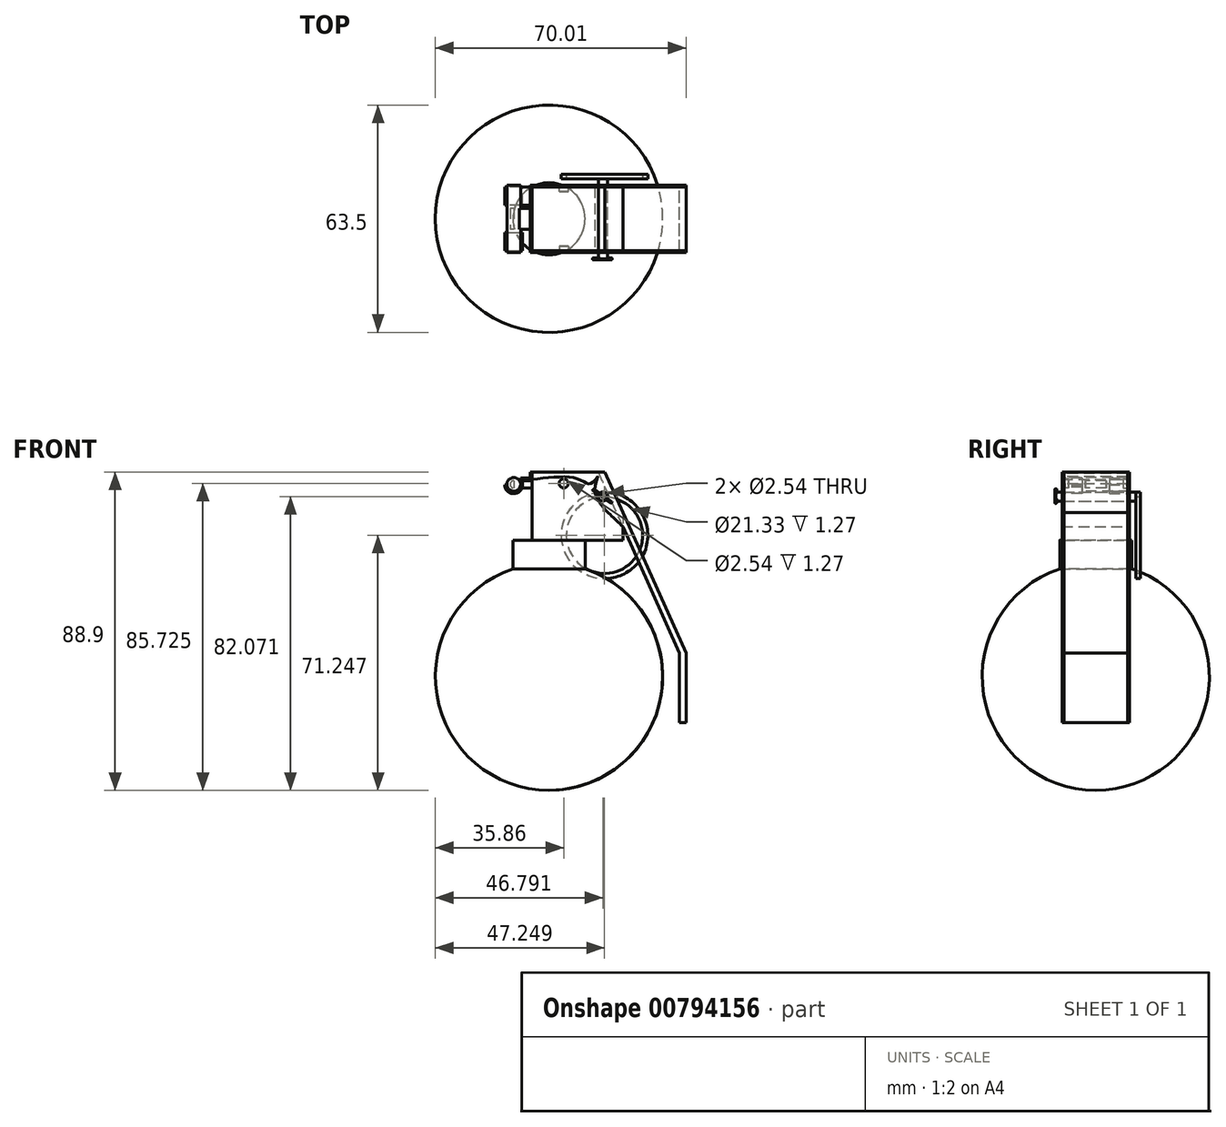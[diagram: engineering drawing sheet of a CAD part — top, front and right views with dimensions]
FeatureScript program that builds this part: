
annotation { "Feature Type Name" : "Feature", "Feature Type Description" : "" }
export const myFeature = defineFeature(function(context is Context, id is Id, definition is map)
    precondition{}
    {
        {
            var Q0;
            Q0=qCreatedBy(makeId("Front.planeOp"),FACE);
            var sketch = newSketch(context, id + "F0", { "sketchPlane" : qUnion([Q0])});
            skCircle(sketch, "E0", {"center": v(0, 0) * mm, "radius": 31.75 * mm});
            skLineSegment(sketch, "E1", {"start": v(0, 31.75) * mm, "end": v(0, -31.75) * mm});
            skSolve(sketch);
        }
        {
            var Q0;
            {var subQ0=sQuery(id+"F0.wireOp",EDGE,"E1");Q0=makeQuery(id+"F0.imprint","IMPRINT",FACE,{"disambiguationData":[TD([[makeQuery(id+"F0.imprint","IMPRINT",EDGE,{"derivedFrom":subQ0}),-1.0]])]});}
            var Q1;
            Q1=sQuery(id+"F0.wireOp",EDGE,"E1");
            revolve(context, id + "F1", {"surfaceOperationType" : NewSurfaceOperationType.NEW, "entities" : qUnion([Q0]), "axis" : qUnion([Q1]), "revolveType" : RevolveType.FULL});
        }
        {
            var Q0;
            Q0=qCreatedBy(makeId("Top.planeOp"),FACE);
            var sketch = newSketch(context, id + "F2", { "sketchPlane" : qUnion([Q0])});
            skCircle(sketch, "E2", {"center": v(0, 0) * mm, "radius": 10.07 * mm});
            skSolve(sketch);
        }
        {
            var Q0;
            Q0 = qSketchRegion(id + "F2", true);
            extrude(context, id + "F3", {"entities" : qUnion([Q0]), "operationType" : NewBodyOperationType.ADD, "depth" : 38.1 * mm, "offsetDistance" : 25.4 * mm});
        }
        {
            var Q0;
            Q0=makeQuery(id+"F3.opExtrude","CAP_FACE",FACE,{"disambiguationData":[OSD([sQuery(id+"F2.wireOp",EDGE,"E2")])],"isStart":false});
            var sketch = newSketch(context, id + "F4", { "sketchPlane" : qUnion([Q0])});
            skLineSegment(sketch, "E3.bottom", {"start": v(-4.78, 8.87) * mm, "end": v(20.62, 8.87) * mm});
            skLineSegment(sketch, "E3.top", {"start": v(-4.78, -8.87) * mm, "end": v(20.62, -8.87) * mm});
            skLineSegment(sketch, "E3.left", {"start": v(-4.78, 8.87) * mm, "end": v(-4.78, -8.87) * mm});
            skLineSegment(sketch, "E3.right", {"start": v(20.62, 8.87) * mm, "end": v(20.62, -8.87) * mm});
            skSolve(sketch);
        }
        {
            var Q0;
            {var subQ0=sQuery(id+"F4.wireOp",EDGE,"E3.left");Q0=makeQuery(id+"F4.imprint","IMPRINT",FACE,{"disambiguationData":[TD([[makeQuery(id+"F4.imprint","IMPRINT",EDGE,{"derivedFrom":subQ0}),1.0]])]});}
            var Q1;
            {var subQ0=sQuery(id+"F4.wireOp",EDGE,"E3.right");Q1=makeQuery(id+"F4.imprint","IMPRINT",FACE,{"disambiguationData":[TD([[makeQuery(id+"F4.imprint","IMPRINT",EDGE,{"derivedFrom":subQ0}),-1.0]])]});}
            extrude(context, id + "F5", {"entities" : qUnion([Q0, Q1]), "operationType" : NewBodyOperationType.ADD, "depth" : 19.05 * mm, "offsetDistance" : 25.4 * mm});
        }
        {
            var Q0;
            Q0=makeQuery(id+"F5.opExtrude","SWEPT_FACE",FACE,{"disambiguationData":[OSD([sQuery(id+"F4.wireOp",EDGE,"E3.bottom")])]});
            var sketch = newSketch(context, id + "F6", { "sketchPlane" : qUnion([Q0])});
            skLineSegment(sketch, "E4", {"start": v(-20.62, 41.9) * mm, "end": v(-13.77, 57.15) * mm});
            skLineSegment(sketch, "E5", {"start": v(-13.77, 57.15) * mm, "end": v(-15.54, 57.15) * mm});
            skLineSegment(sketch, "E6", {"start": v(-15.54, 57.15) * mm, "end": v(-38.26, 6.55) * mm});
            skLineSegment(sketch, "E7", {"start": v(-38.26, 6.55) * mm, "end": v(-38.26, -12.78) * mm});
            skLineSegment(sketch, "E8", {"start": v(-38.26, -12.78) * mm, "end": v(-36.4, -12.78) * mm});
            skLineSegment(sketch, "E9", {"start": v(-36.4, -12.78) * mm, "end": v(-36.4, 6.55) * mm});
            skLineSegment(sketch, "E10", {"start": v(-36.4, 6.55) * mm, "end": v(-20.62, 41.9) * mm});
            skPoint(sketch, "E11.4.internal.snap0", {"position": v(-7.92, 57.15) * mm});
            skFitSpline(sketch, "E11", {"points": [v(-20.62, 41.9) * mm, v(-12.84, 51.9) * mm, v(-13.59, 55.87) * mm, v(-11.77, 53.97) * mm, v(-7.92, 55.3) * mm, v(4.78, 55.13) * mm], "startDerivative": vector(37.94, 36.96) * mm, "endDerivative": vector(48.27, -4.72) * mm});
            skCircle(sketch, "E12", {"center": v(-15.04, 50.32) * mm, "radius": 1.27 * mm});
            skSolve(sketch);
        }
        {
            var Q0;
            Q0 = qSketchRegion(id + "F6", true);
            extrude(context, id + "F7", {"entities" : qUnion([Q0]), "oppositeDirection" : true, "depth" : 17.78 * mm, "offsetDistance" : 25.4 * mm});
        }
        {
            var Q0;
            {var subQ0=sQuery(id+"F6.wireOp",EDGE,"E6");var subQ1=sQuery(id+"F4.wireOp",EDGE,"E3.bottom");var subQ2=makeQuery(id+"F5.opExtrude","CAP_EDGE",EDGE,{"disambiguationData":[OSD([subQ1])],"isStart":false});var subQ3=makeQuery(id+"F6.imprint","INTERSECT",VERTEX,{"derivedFrom":[subQ2,sQuery(id+"F6.wireOp",EDGE,"E5"),subQ0]});Q0=makeQuery(id+"F6.imprint","IMPRINT",FACE,{"disambiguationData":[TD([[makeQuery(id+"F6.imprint","IMPRINT",EDGE,{"disambiguationData":[TD([[subQ3,-1.0]])],"derivedFrom":subQ0}),-1.0]])]});}
            extrude(context, id + "F8", {"entities" : qUnion([Q0]), "operationType" : NewBodyOperationType.REMOVE, "oppositeDirection" : true, "depth" : 25.4 * mm, "offsetDistance" : 25.4 * mm});
        }
        {
            var Q0;
            {var subQ0=sQuery(id+"F6.wireOp",EDGE,"E4");Q0=makeQuery(id+"F6.imprint","IMPRINT",FACE,{"disambiguationData":[TD([[makeQuery(id+"F6.imprint","IMPRINT",EDGE,{"derivedFrom":subQ0}),1.0]])]});}
            var Q1;
            {var subQ0=sQuery(id+"F6.wireOp",EDGE,"E4");Q1=makeQuery(id+"F6.imprint","IMPRINT",FACE,{"disambiguationData":[TD([[makeQuery(id+"F6.imprint","IMPRINT",EDGE,{"derivedFrom":subQ0}),-1.0]])]});}
            var Q2;
            {var subQ0=sQuery(id+"F6.wireOp",EDGE,"E7");Q2=makeQuery(id+"F6.imprint","IMPRINT",FACE,{"disambiguationData":[TD([[makeQuery(id+"F6.imprint","IMPRINT",EDGE,{"derivedFrom":subQ0}),1.0]])]});}
            extrude(context, id + "F9", {"entities" : qUnion([Q0, Q1, Q2]), "depth" : 0.5 * mm, "offsetDistance" : 25.4 * mm});
        }
        {
            var Q0;
            {var subQ0=sQuery(id+"F6.wireOp",EDGE,"E4");Q0=makeQuery(id+"F6.imprint","IMPRINT",FACE,{"disambiguationData":[TD([[makeQuery(id+"F6.imprint","IMPRINT",EDGE,{"derivedFrom":subQ0}),-1.0]])]});}
            var Q1;
            {var subQ0=sQuery(id+"F6.wireOp",EDGE,"E4");Q1=makeQuery(id+"F6.imprint","IMPRINT",FACE,{"disambiguationData":[TD([[makeQuery(id+"F6.imprint","IMPRINT",EDGE,{"derivedFrom":subQ0}),1.0]])]});}
            var Q2;
            {var subQ0=sQuery(id+"F6.wireOp",EDGE,"E7");Q2=makeQuery(id+"F6.imprint","IMPRINT",FACE,{"disambiguationData":[TD([[makeQuery(id+"F6.imprint","IMPRINT",EDGE,{"derivedFrom":subQ0}),1.0]])]});}
            extrude(context, id + "F10", {"entities" : qUnion([Q0, Q1, Q2]), "oppositeDirection" : true, "depth" : 18.29 * mm, "offsetDistance" : 25.4 * mm});
        }
        {
            var Q0;
            Q0=makeQuery(id+"F5.opExtrude","SWEPT_FACE",FACE,{"disambiguationData":[OSD([sQuery(id+"F4.wireOp",EDGE,"E3.left")])]});
            var sketch = newSketch(context, id + "F11", { "sketchPlane" : qUnion([Q0])});
            skLineSegment(sketch, "E13", {"start": v(-9.66, 56.79) * mm, "end": v(9.7, 56.79) * mm});
            skLineSegment(sketch, "E14.bottom", {"start": v(-2.95, 54.72) * mm, "end": v(2.95, 54.72) * mm});
            skLineSegment(sketch, "E14.top", {"start": v(-2.95, 52.7) * mm, "end": v(2.95, 52.7) * mm});
            skLineSegment(sketch, "E14.left", {"start": v(-2.95, 54.72) * mm, "end": v(-2.95, 52.7) * mm});
            skLineSegment(sketch, "E14.right", {"start": v(2.95, 54.72) * mm, "end": v(2.95, 52.7) * mm});
            skPoint(sketch, "E14.middle", {"position": v(0, 53.71) * mm});
            skSolve(sketch);
        }
        {
            var Q0;
            Q0=makeQuery(id+"F9.opExtrude","SWEPT_FACE",FACE,{"disambiguationData":[OSD([sQuery(id+"F2.wireOp",EDGE,"E2"),sQuery(id+"F4.wireOp",EDGE,"E3.bottom"),sQuery(id+"F4.wireOp",EDGE,"E3.left")])]});
            var Q1;
            {var subQ1=sQuery(id+"F4.wireOp",EDGE,"E3.left");var subQ7=makeQuery(id+"F5.opExtrude","CAP_EDGE",EDGE,{"disambiguationData":[OSD([subQ1])],"isStart":false});Q1=makeQuery(id+"F11.imprint","IMPRINT",FACE,{"disambiguationData":[TD([[makeQuery(id+"F11.imprint","IMPRINT",EDGE,{"derivedFrom":subQ7}),-1.0]])]});}
            var Q2;
            Q2=makeQuery(id+"F10.opExtrude","SWEPT_FACE",FACE,{"disambiguationData":[OSD([sQuery(id+"F2.wireOp",EDGE,"E2"),sQuery(id+"F4.wireOp",EDGE,"E3.bottom"),sQuery(id+"F4.wireOp",EDGE,"E3.left")])]});
            extrude(context, id + "F12", {"entities" : qUnion([Q0, Q1, Q2]), "depth" : 0.5 * mm, "offsetDistance" : 25.4 * mm});
        }
        {
            var Q0;
            Q0=makeQuery(id+"F11.imprint","IMPRINT",FACE,{"disambiguationData":[TD([[makeQuery(id+"F11.imprint","IMPRINT",EDGE,{"derivedFrom":sQuery(id+"F11.wireOp",EDGE,"E14.bottom")}),-1.0]])]});
            extrude(context, id + "F13", {"entities" : qUnion([Q0]), "operationType" : NewBodyOperationType.ADD, "depth" : 5.08 * mm, "offsetDistance" : 25.4 * mm});
        }
        {
            var Q0;
            Q0=makeQuery(id+"F13.opExtrude","CAP_FACE",FACE,{"disambiguationData":[OSD([sQuery(id+"F11.wireOp",EDGE,"E14.bottom"),sQuery(id+"F11.wireOp",EDGE,"E14.top"),sQuery(id+"F11.wireOp",EDGE,"E14.left"),sQuery(id+"F11.wireOp",EDGE,"E14.right")])],"isStart":false});
            var sketch = newSketch(context, id + "F14", { "sketchPlane" : qUnion([Q0])});
            skLineSegment(sketch, "E15", {"start": v(-2.95, 53.71) * mm, "end": v(2.95, 53.71) * mm});
            skLineSegment(sketch, "E16", {"start": v(2.95, 53.71) * mm, "end": v(9.42, 53.71) * mm});
            skLineSegment(sketch, "E17", {"start": v(9.42, 53.71) * mm, "end": v(-9.38, 53.71) * mm});
            skLineSegment(sketch, "E18", {"start": v(-9.38, 53.71) * mm, "end": v(-9.38, 51.8) * mm});
            skLineSegment(sketch, "E19", {"start": v(-9.38, 51.8) * mm, "end": v(9.42, 51.8) * mm});
            skLineSegment(sketch, "E20", {"start": v(9.42, 53.71) * mm, "end": v(9.42, 51.8) * mm});
            skSolve(sketch);
        }
        {
            var Q0;
            {var subQ0=sQuery(id+"F14.wireOp",EDGE,"E18");Q0=makeQuery(id+"F14.imprint","IMPRINT",FACE,{"disambiguationData":[TD([[makeQuery(id+"F14.imprint","IMPRINT",EDGE,{"derivedFrom":subQ0}),1.0]])]});}
            var Q1;
            Q1=sQuery(id+"F14.wireOp",EDGE,"E17");
            revolve(context, id + "F15", {"operationType" : NewBodyOperationType.ADD, "surfaceOperationType" : NewSurfaceOperationType.NEW, "entities" : qUnion([Q0]), "axis" : qUnion([Q1]), "revolveType" : RevolveType.FULL});
        }
        {
            var Q0;
            Q0=makeQuery(id+"F5.opExtrude","SWEPT_FACE",FACE,{"disambiguationData":[OSD([sQuery(id+"F4.wireOp",EDGE,"E3.bottom")])]});
            var sketch = newSketch(context, id + "F16", { "sketchPlane" : qUnion([Q0])});
            skLineSegment(sketch, "E21.left", {"start": v(4.78, 57.15) * mm, "end": v(4.78, 55.04) * mm});
            skArc(sketch, "E22", {"start": v(7.95, 53.66) * mm, "mid": v(9.85, 51.83) * mm, "end": v(11.78, 53.63) * mm});
            skArc(sketch, "E23", {"start": v(7.4, 53.64) * mm, "mid": v(9.87, 51.12) * mm, "end": v(12.38, 53.59) * mm});
            skLineSegment(sketch, "E24", {"start": v(7.95, 53.66) * mm, "end": v(7.4, 53.64) * mm});
            skLineSegment(sketch, "E25", {"start": v(11.78, 53.63) * mm, "end": v(12.38, 53.59) * mm});
            skLineSegment(sketch, "E26.bottom", {"start": v(4.78, 55.14) * mm, "end": v(7.4, 55.14) * mm});
            skLineSegment(sketch, "E26.top", {"start": v(4.78, 55.53) * mm, "end": v(7.4, 55.53) * mm});
            skLineSegment(sketch, "E26.left", {"start": v(4.78, 55.14) * mm, "end": v(4.78, 55.53) * mm});
            skLineSegment(sketch, "E26.right", {"start": v(7.4, 55.14) * mm, "end": v(7.4, 55.53) * mm});
            skLineSegment(sketch, "E27.bottom", {"start": v(7.4, 55.53) * mm, "end": v(7.95, 55.53) * mm});
            skLineSegment(sketch, "E27.top", {"start": v(7.4, 53.66) * mm, "end": v(7.95, 53.66) * mm});
            skLineSegment(sketch, "E27.left", {"start": v(7.4, 55.53) * mm, "end": v(7.4, 53.66) * mm});
            skLineSegment(sketch, "E27.right", {"start": v(7.95, 55.53) * mm, "end": v(7.95, 53.66) * mm});
            skLineSegment(sketch, "E28", {"start": v(7.4, 53.66) * mm, "end": v(7.4, 53.64) * mm});
            skCircle(sketch, "E29", {"center": v(-4.11, 53.98) * mm, "radius": 1.27 * mm});
            skPoint(sketch, "E29.first.point", {"position": v(-4.07, 55.24) * mm});
            skPoint(sketch, "E29.second.point", {"position": v(-5.25, 53.4) * mm});
            skPoint(sketch, "E29.third.point", {"position": v(-2.9, 53.56) * mm});
            skSolve(sketch);
        }
        {
            var Q0;
            {var subQ0=sQuery(id+"F16.wireOp",EDGE,"E26.bottom");Q0=makeQuery(id+"F16.imprint","IMPRINT",FACE,{"disambiguationData":[TD([[makeQuery(id+"F16.imprint","IMPRINT",EDGE,{"derivedFrom":subQ0}),1.0]])]});}
            var Q1;
            {var subQ3=sQuery(id+"F16.wireOp",EDGE,"E27.bottom");Q1=makeQuery(id+"F16.imprint","IMPRINT",FACE,{"disambiguationData":[TD([[makeQuery(id+"F16.imprint","IMPRINT",EDGE,{"derivedFrom":subQ3}),-1.0]])]});}
            var Q2;
            Q2=makeQuery(id+"F16.imprint","IMPRINT",FACE,{"disambiguationData":[TD([[makeQuery(id+"F16.imprint","IMPRINT",EDGE,{"derivedFrom":sQuery(id+"F16.wireOp",EDGE,"E22")}),-1.0]])]});
            extrude(context, id + "F17", {"entities" : qUnion([Q0, Q1, Q2]), "oppositeDirection" : true, "depth" : 5.08 * mm, "offsetDistance" : 25.4 * mm});
        }
        {
            var Q0;
            Q0=makeQuery(id+"F5.opExtrude","SWEPT_FACE",FACE,{"disambiguationData":[OSD([sQuery(id+"F4.wireOp",EDGE,"E3.top")])]});
            var sketch = newSketch(context, id + "F18", { "sketchPlane" : qUnion([Q0])});
            skCircle(sketch, "E30", {"center": v(13.74, 50.52) * mm, "radius": 1.14 * mm});
            skPoint(sketch, "E30.first.point", {"position": v(13.7, 51.66) * mm});
            skPoint(sketch, "E30.second.point", {"position": v(13.1, 49.57) * mm});
            skPoint(sketch, "E30.third.point", {"position": v(14.83, 50.19) * mm});
            skCircle(sketch, "E31", {"center": v(4.11, 53.98) * mm, "radius": 1.27 * mm});
            skPoint(sketch, "E31.first.point", {"position": v(4.27, 55.24) * mm});
            skPoint(sketch, "E31.second.point", {"position": v(2.96, 53.44) * mm});
            skPoint(sketch, "E31.third.point", {"position": v(5.2, 53.32) * mm});
            skLineSegment(sketch, "E32.MirrorCS", {"start": v(-7.4, 55.13) * mm, "end": v(-7.4, 55.53) * mm});
            skLineSegment(sketch, "E33.MirrorCS", {"start": v(-7.95, 53.65) * mm, "end": v(-7.4, 53.63) * mm});
            skLineSegment(sketch, "E34.MirrorCS", {"start": v(-7.4, 53.65) * mm, "end": v(-7.95, 53.65) * mm});
            skLineSegment(sketch, "E35.MirrorCS", {"start": v(-7.4, 53.65) * mm, "end": v(-7.4, 53.63) * mm});
            skLineSegment(sketch, "E36.MirrorCS", {"start": v(-7.4, 55.53) * mm, "end": v(-7.95, 55.53) * mm});
            skLineSegment(sketch, "E37.MirrorCS", {"start": v(-11.77, 53.62) * mm, "end": v(-12.37, 53.58) * mm});
            skLineSegment(sketch, "E38.MirrorCS", {"start": v(-4.77, 55.13) * mm, "end": v(-4.77, 55.53) * mm});
            skLineSegment(sketch, "E39.MirrorCS", {"start": v(-4.77, 55.13) * mm, "end": v(-7.4, 55.13) * mm});
            skArc(sketch, "E40.MirrorCS", {"start": v(-7.95, 53.65) * mm, "mid": v(-9.85, 51.83) * mm, "end": v(-11.77, 53.62) * mm});
            skLineSegment(sketch, "E41.MirrorCS", {"start": v(-4.77, 55.53) * mm, "end": v(-7.4, 55.53) * mm});
            skArc(sketch, "E42.MirrorCS", {"start": v(-7.4, 53.63) * mm, "mid": v(-9.86, 51.12) * mm, "end": v(-12.37, 53.58) * mm});
            skLineSegment(sketch, "E43.MirrorCS", {"start": v(-7.4, 55.53) * mm, "end": v(-7.4, 53.65) * mm});
            skLineSegment(sketch, "E44.MirrorCS", {"start": v(-7.95, 55.53) * mm, "end": v(-7.95, 53.65) * mm});
            skSolve(sketch);
        }
        {
            var Q0;
            Q0=makeQuery(id+"F6.imprint","IMPRINT",FACE,{"disambiguationData":[TD([[makeQuery(id+"F6.imprint","IMPRINT",EDGE,{"derivedFrom":sQuery(id+"F6.wireOp",EDGE,"E12")}),1.0]])]});
            extrude(context, id + "F19", {"entities" : qUnion([Q0]), "depth" : 2.3 * mm, "offsetDistance" : 25.4 * mm});
        }
        {
            var Q0;
            Q0=makeQuery(id+"F19.opExtrude","CAP_FACE",FACE,{"disambiguationData":[OSD([sQuery(id+"F6.wireOp",EDGE,"E12")])],"isStart":false});
            var sketch = newSketch(context, id + "F20", { "sketchPlane" : qUnion([Q0])});
            skCircle(sketch, "E45", {"center": v(-15.5, 39.5) * mm, "radius": 12.1 * mm});
            skPoint(sketch, "E45.first.point", {"position": v(-15.08, 51.6) * mm});
            skPoint(sketch, "E45.second.point", {"position": v(-24.22, 31.11) * mm});
            skPoint(sketch, "E45.third.point", {"position": v(-3.94, 35.92) * mm});
            skCircle(sketch, "E46", {"center": v(-15.5, 39.5) * mm, "radius": 10.67 * mm});
            skSolve(sketch);
        }
        {
            var Q0;
            {var subQ0=sQuery(id+"F20.wireOp",EDGE,"E45");var subQ1=makeQuery(id+"F19.opExtrude","CAP_EDGE",EDGE,{"disambiguationData":[OSD([sQuery(id+"F6.wireOp",EDGE,"E12")])],"isStart":false});var subQ2=makeQuery(id+"F20.imprint","INTERSECT",VERTEX,{"disambiguationData":[OD(0.0)],"derivedFrom":[subQ1,subQ0]});Q0=makeQuery(id+"F20.imprint","IMPRINT",FACE,{"disambiguationData":[TD([[makeQuery(id+"F20.imprint","IMPRINT",EDGE,{"disambiguationData":[TD([[subQ2,1.0]])],"derivedFrom":subQ0}),1.0]])]});}
            var Q1;
            {var subQ0=sQuery(id+"F20.wireOp",EDGE,"E45");var subQ1=makeQuery(id+"F19.opExtrude","CAP_EDGE",EDGE,{"disambiguationData":[OSD([sQuery(id+"F6.wireOp",EDGE,"E12")])],"isStart":false});var subQ2=makeQuery(id+"F20.imprint","INTERSECT",VERTEX,{"disambiguationData":[OD(0.0)],"derivedFrom":[subQ1,subQ0]});Q1=makeQuery(id+"F20.imprint","IMPRINT",FACE,{"disambiguationData":[TD([[makeQuery(id+"F20.imprint","IMPRINT",EDGE,{"disambiguationData":[TD([[subQ2,-1.0]])],"derivedFrom":subQ0}),1.0]])]});}
            extrude(context, id + "F21", {"entities" : qUnion([Q0, Q1]), "operationType" : NewBodyOperationType.ADD, "depth" : 1.27 * mm, "offsetDistance" : 25.4 * mm});
        }
        {
            var Q0;
            Q0=makeQuery(id+"F7.opExtrude","CAP_FACE",FACE,{"disambiguationData":[OSD([sQuery(id+"F6.wireOp",EDGE,"E12")])],"isStart":false});
            extrude(context, id + "F22", {"entities" : qUnion([Q0]), "depth" : 2.3 * mm, "offsetDistance" : 25.4 * mm});
        }
        {
            var Q0;
            Q0=makeQuery(id+"F22.opExtrude","CAP_FACE",FACE,{"disambiguationData":[OSD([sQuery(id+"F6.wireOp",EDGE,"E12")])],"isStart":false});
            var sketch = newSketch(context, id + "F23", { "sketchPlane" : qUnion([Q0])});
            skLineSegment(sketch, "E47", {"start": v(15.04, 50.32) * mm, "end": v(12.3, 52.3) * mm});
            skLineSegment(sketch, "E48", {"start": v(12.3, 52.3) * mm, "end": v(17.46, 48.58) * mm});
            skLineSegment(sketch, "E49", {"start": v(12.3, 52.3) * mm, "end": v(12.46, 52.5) * mm});
            skLineSegment(sketch, "E50", {"start": v(12.46, 52.5) * mm, "end": v(17.6, 48.79) * mm});
            skLineSegment(sketch, "E51", {"start": v(17.6, 48.79) * mm, "end": v(17.46, 48.58) * mm});
            skSolve(sketch);
        }
        {
            var Q0;
            Q0 = qSketchRegion(id + "F23", true);
            var Q1;
            Q1=sQuery(id+"F23.wireOp",EDGE,"E48");
            revolve(context, id + "F24", {"operationType" : NewBodyOperationType.ADD, "surfaceOperationType" : NewSurfaceOperationType.NEW, "entities" : qUnion([Q0]), "axis" : qUnion([Q1]), "revolveType" : RevolveType.FULL});
        }
        {
            var Q0;
            Q0=makeQuery(id+"F16.imprint","IMPRINT",FACE,{"disambiguationData":[TD([[makeQuery(id+"F16.imprint","IMPRINT",EDGE,{"derivedFrom":sQuery(id+"F16.wireOp",EDGE,"E24")}),-1.0]])]});
            extrude(context, id + "F25", {"entities" : qUnion([Q0]), "oppositeDirection" : true, "depth" : 5.08 * mm, "offsetDistance" : 25.4 * mm});
        }
        {
            var Q0;
            Q0=makeQuery(id+"F18.imprint","IMPRINT",FACE,{"disambiguationData":[TD([[makeQuery(id+"F18.imprint","IMPRINT",EDGE,{"derivedFrom":sQuery(id+"F18.wireOp",EDGE,"E31")}),1.0]])]});
            extrude(context, id + "F26", {"entities" : qUnion([Q0]), "operationType" : NewBodyOperationType.REMOVE, "oppositeDirection" : true, "depth" : 1.27 * mm, "offsetDistance" : 25.4 * mm});
        }
        {
            var Q0;
            Q0=makeQuery(id+"F16.imprint","IMPRINT",FACE,{"disambiguationData":[TD([[makeQuery(id+"F16.imprint","IMPRINT",EDGE,{"derivedFrom":sQuery(id+"F16.wireOp",EDGE,"E29")}),1.0]])]});
            extrude(context, id + "F27", {"entities" : qUnion([Q0]), "operationType" : NewBodyOperationType.REMOVE, "oppositeDirection" : true, "depth" : 1.27 * mm, "offsetDistance" : 25.4 * mm});
        }
        {
            var Q0;
            Q0=makeQuery(id+"F18.imprint","IMPRINT",FACE,{"disambiguationData":[TD([[makeQuery(id+"F18.imprint","IMPRINT",EDGE,{"derivedFrom":sQuery(id+"F18.wireOp",EDGE,"E33.MirrorCS")}),-1.0]])]});
            var Q1;
            {var subQ3=sQuery(id+"F18.wireOp",EDGE,"E34.MirrorCS");Q1=makeQuery(id+"F18.imprint","IMPRINT",FACE,{"disambiguationData":[TD([[makeQuery(id+"F18.imprint","IMPRINT",EDGE,{"derivedFrom":subQ3}),-1.0]])]});}
            var Q2;
            Q2=makeQuery(id+"F18.imprint","IMPRINT",FACE,{"disambiguationData":[TD([[makeQuery(id+"F18.imprint","IMPRINT",EDGE,{"derivedFrom":sQuery(id+"F18.wireOp",EDGE,"E33.MirrorCS")}),1.0]])]});
            var Q3;
            {var subQ0=sQuery(id+"F18.wireOp",EDGE,"E43.MirrorCS");var subQ1=sQuery(id+"F18.wireOp",EDGE,"E39.MirrorCS");var subQ2=makeQuery(id+"F18.imprint","INTERSECT",VERTEX,{"derivedFrom":[subQ1,subQ0]});Q3=makeQuery(id+"F18.imprint","IMPRINT",FACE,{"disambiguationData":[TD([[makeQuery(id+"F18.imprint","IMPRINT",EDGE,{"disambiguationData":[TD([[subQ2,1.0]])],"derivedFrom":subQ0}),1.0]])]});}
            extrude(context, id + "F28", {"entities" : qUnion([Q0, Q1, Q2, Q3]), "operationType" : NewBodyOperationType.ADD, "oppositeDirection" : true, "depth" : 5.08 * mm, "offsetDistance" : 25.4 * mm});
        }
        {
            var Q0;
            Q0=makeQuery(id+"F16.imprint","IMPRINT",FACE,{"disambiguationData":[TD([[makeQuery(id+"F16.imprint","IMPRINT",EDGE,{"derivedFrom":sQuery(id+"F16.wireOp",EDGE,"E29")}),1.0]])]});
            extrude(context, id + "F29", {"entities" : qUnion([Q0]), "operationType" : NewBodyOperationType.REMOVE, "oppositeDirection" : true, "depth" : 1.27 * mm, "offsetDistance" : 25.4 * mm});
        }
        {
            var Q0;
            Q0=makeQuery(id+"F5.opExtrude","SWEPT_FACE",FACE,{"disambiguationData":[OSD([sQuery(id+"F4.wireOp",EDGE,"E3.top")])]});
            var sketch = newSketch(context, id + "F30", { "sketchPlane" : qUnion([Q0])});
            skCircle(sketch, "E52", {"center": v(4.1, 53.98) * mm, "radius": 1.27 * mm});
            skSolve(sketch);
        }
        {
            var Q0;
            Q0 = qSketchRegion(id + "F30", true);
            extrude(context, id + "F31", {"entities" : qUnion([Q0]), "operationType" : NewBodyOperationType.REMOVE, "oppositeDirection" : true, "depth" : 1.27 * mm, "offsetDistance" : 25.4 * mm});
        }
    });
